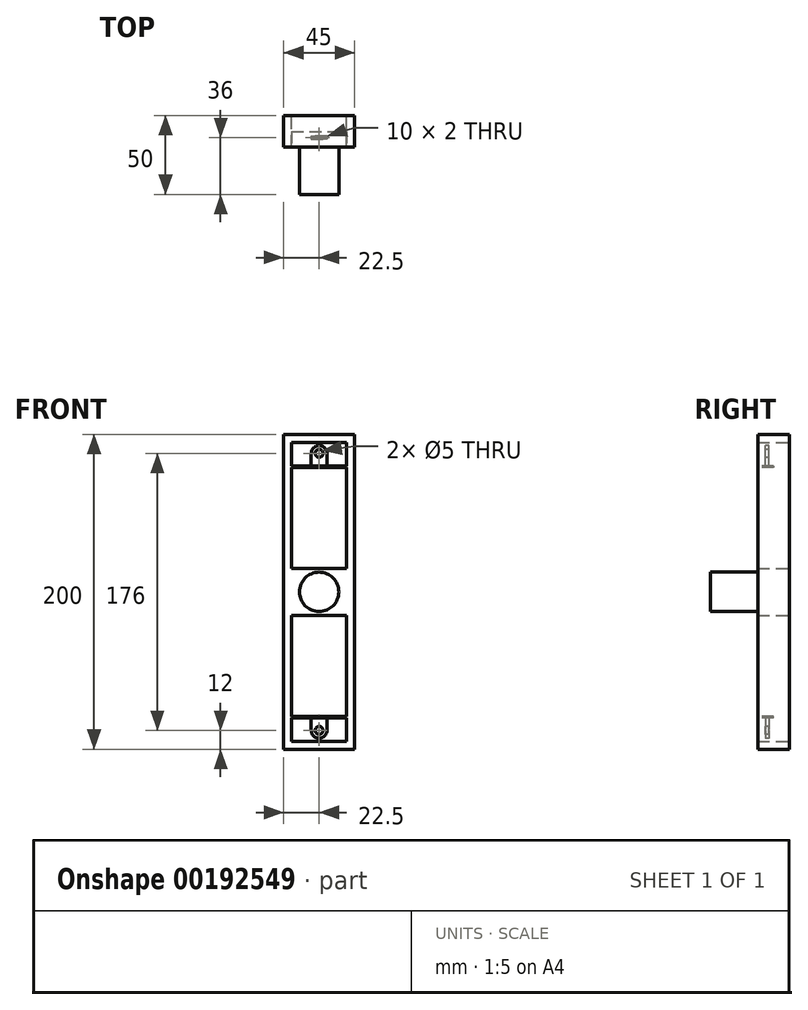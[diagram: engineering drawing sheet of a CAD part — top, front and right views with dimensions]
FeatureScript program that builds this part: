
annotation { "Feature Type Name" : "Feature", "Feature Type Description" : "" }
export const myFeature = defineFeature(function(context is Context, id is Id, definition is map)
    precondition{}
    {
        {
            var Q0;
            Q0=qCreatedBy(makeId("Front.planeOp"),FACE);
            var sketch = newSketch(context, id + "F0", { "sketchPlane" : qUnion([Q0])});
            skCircle(sketch, "E0", {"center": v(0, 0) * mm, "radius": 12.5 * mm});
            skSolve(sketch);
        }
        {
            var Q0;
            Q0=qSketchRegion(id+"F0",true);
            extrude(context, id + "F1", {"entities" : qUnion([Q0]), "depth" : 40 * mm});
        }
        {
            var Q0;
            Q0=qCreatedBy(makeId("Front.planeOp"),FACE);
            cPlane(context, id + "F2", {"entities" : qUnion([Q0]), "cplaneType" : CPlaneType.OFFSET, "offset" : 10 * mm, "width" : 150 * mm, "height" : 150 * mm});
        }
        {
            var Q0;
            Q0=qCreatedBy(id+"F2.planeOp",FACE);
            var sketch = newSketch(context, id + "F3", { "sketchPlane" : qUnion([Q0])});
            skLineSegment(sketch, "E1.bottom", {"start": v(-22.5, -100) * mm, "end": v(22.5, -100) * mm});
            skLineSegment(sketch, "E1.top", {"start": v(-22.5, 100) * mm, "end": v(22.5, 100) * mm});
            skLineSegment(sketch, "E1.left", {"start": v(-22.5, -100) * mm, "end": v(-22.5, 100) * mm});
            skLineSegment(sketch, "E1.right", {"start": v(22.5, -100) * mm, "end": v(22.5, 100) * mm});
            skPoint(sketch, "E1.middle", {"position": v(0, 0) * mm});
            skSolve(sketch);
        }
        {
            var Q0;
            Q0=qSketchRegion(id+"F3",true);
            extrude(context, id + "F4", {"entities" : qUnion([Q0]), "operationType" : NewBodyOperationType.ADD, "oppositeDirection" : true, "depth" : 20 * mm});
        }
        {
            var Q0;
            Q0=makeQuery(id+"F4.opExtrude","CAP_FACE",FACE,{"disambiguationData":[OSD([sQuery(id+"F3.wireOp",EDGE,"E1.bottom"),sQuery(id+"F3.wireOp",EDGE,"E1.top"),sQuery(id+"F3.wireOp",EDGE,"E1.left"),sQuery(id+"F3.wireOp",EDGE,"E1.right")])],"isStart":false});
            var sketch = newSketch(context, id + "F5", { "sketchPlane" : qUnion([Q0])});
            skLineSegment(sketch, "E2.bottom", {"start": v(-17.5, 95) * mm, "end": v(17.5, 95) * mm});
            skLineSegment(sketch, "E2.top", {"start": v(-17.5, 15) * mm, "end": v(17.5, 15) * mm});
            skLineSegment(sketch, "E2.left", {"start": v(-17.5, 95) * mm, "end": v(-17.5, 15) * mm});
            skLineSegment(sketch, "E2.right", {"start": v(17.5, 95) * mm, "end": v(17.5, 15) * mm});
            skLineSegment(sketch, "E3.bottom", {"start": v(-17.5, -15) * mm, "end": v(17.5, -15) * mm});
            skLineSegment(sketch, "E3.top", {"start": v(-17.5, -95) * mm, "end": v(17.5, -95) * mm});
            skLineSegment(sketch, "E3.left", {"start": v(-17.5, -15) * mm, "end": v(-17.5, -95) * mm});
            skLineSegment(sketch, "E3.right", {"start": v(17.5, -15) * mm, "end": v(17.5, -95) * mm});
            skSolve(sketch);
        }
        {
            var Q0;
            Q0 = qSketchRegion(id + "F5", true);
            extrude(context, id + "F6", {"entities" : qUnion([Q0]), "operationType" : NewBodyOperationType.REMOVE, "oppositeDirection" : true, "depth" : 25 * mm});
        }
        {
            var Q0;
            Q0=qCreatedBy(makeId("Top.planeOp"),FACE);
            cPlane(context, id + "F7", {"entities" : qUnion([Q0]), "cplaneType" : CPlaneType.OFFSET, "offset" : 80 * mm, "width" : 150 * mm, "height" : 150 * mm});
        }
        {
            var Q0;
            Q0=qCreatedBy(makeId("Top.planeOp"),FACE);
            cPlane(context, id + "F8", {"entities" : qUnion([Q0]), "cplaneType" : CPlaneType.OFFSET, "offset" : 80 * mm, "oppositeDirection" : true, "width" : 150 * mm, "height" : 150 * mm});
        }
        {
            var Q0;
            Q0=qCreatedBy(id+"F7.planeOp",FACE);
            var sketch = newSketch(context, id + "F9", { "sketchPlane" : qUnion([Q0])});
            skLineSegment(sketch, "E4.bottom", {"start": v(-22.5, -10) * mm, "end": v(22.5, -10) * mm});
            skLineSegment(sketch, "E4.top", {"start": v(-22.5, 0) * mm, "end": v(22.5, 0) * mm});
            skLineSegment(sketch, "E4.left", {"start": v(-22.5, -10) * mm, "end": v(-22.5, 0) * mm});
            skLineSegment(sketch, "E4.right", {"start": v(22.5, -10) * mm, "end": v(22.5, 0) * mm});
            skSolve(sketch);
        }
        {
            var Q0;
            Q0 = qSketchRegion(id + "F9", true);
            extrude(context, id + "F10", {"entities" : qUnion([Q0]), "operationType" : NewBodyOperationType.ADD, "oppositeDirection" : true, "depth" : 1 * mm});
        }
        {
            var Q0;
            Q0=qCreatedBy(id+"F8.planeOp",FACE);
            var sketch = newSketch(context, id + "F11", { "sketchPlane" : qUnion([Q0])});
            skLineSegment(sketch, "E5.bottom", {"start": v(-22.5, 0) * mm, "end": v(22.5, 0) * mm});
            skLineSegment(sketch, "E5.top", {"start": v(-22.5, -10) * mm, "end": v(22.5, -10) * mm});
            skLineSegment(sketch, "E5.left", {"start": v(-22.5, 0) * mm, "end": v(-22.5, -10) * mm});
            skLineSegment(sketch, "E5.right", {"start": v(22.5, 0) * mm, "end": v(22.5, -10) * mm});
            skSolve(sketch);
        }
        {
            var Q0;
            Q0 = qSketchRegion(id + "F11", true);
            extrude(context, id + "F12", {"entities" : qUnion([Q0]), "operationType" : NewBodyOperationType.ADD, "depth" : 1 * mm});
        }
        {
            var Q0;
            Q0=qCreatedBy(makeId("Front.planeOp"),FACE);
            cPlane(context, id + "F13", {"entities" : qUnion([Q0]), "cplaneType" : CPlaneType.OFFSET, "offset" : 5 * mm, "width" : 150 * mm, "height" : 150 * mm});
        }
        {
            var Q0;
            Q0=qCreatedBy(id+"F13.planeOp",FACE);
            var sketch = newSketch(context, id + "F14", { "sketchPlane" : qUnion([Q0])});
            skLineSegment(sketch, "E6", {"start": v(-5, 80) * mm, "end": v(-5, 88) * mm});
            skArc(sketch, "E7", {"start": v(5, 88) * mm, "mid": v(0, 93) * mm, "end": v(-5, 88) * mm});
            skLineSegment(sketch, "E8", {"start": v(5, 88) * mm, "end": v(5, 80) * mm});
            skLineSegment(sketch, "E9", {"start": v(-5, -80) * mm, "end": v(-5, -88) * mm});
            skArc(sketch, "E10", {"start": v(-5, -88) * mm, "mid": v(0, -93) * mm, "end": v(5, -88) * mm});
            skLineSegment(sketch, "E11", {"start": v(5, -88) * mm, "end": v(5, -80) * mm});
            skLineSegment(sketch, "E12", {"start": v(-5, 80) * mm, "end": v(5, 80) * mm});
            skLineSegment(sketch, "E13", {"start": v(-5, -80) * mm, "end": v(5, -80) * mm});
            skSolve(sketch);
        }
        {
            var Q0;
            Q0 = qSketchRegion(id + "F14", true);
            extrude(context, id + "F15", {"entities" : qUnion([Q0]), "oppositeDirection" : true, "depth" : 2 * mm});
        }
        {
            var Q0;
            Q0=makeQuery(id+"F1.opExtrude","SWEPT_BODY",BODY,{"disambiguationData":[OSD([sQuery(id+"F0.wireOp",EDGE,"E0")])]});
            var Q1;
            Q1=makeQuery(id+"F15.opExtrude","SWEPT_BODY",BODY,{"disambiguationData":[OSD([sQuery(id+"F14.wireOp",EDGE,"E6"),sQuery(id+"F14.wireOp",EDGE,"E7"),sQuery(id+"F14.wireOp",EDGE,"E8"),sQuery(id+"F14.wireOp",EDGE,"E12")])]});
            var Q2;
            Q2=makeQuery(id+"F15.opExtrude","SWEPT_BODY",BODY,{"disambiguationData":[OSD([sQuery(id+"F14.wireOp",EDGE,"E9"),sQuery(id+"F14.wireOp",EDGE,"E10"),sQuery(id+"F14.wireOp",EDGE,"E11"),sQuery(id+"F14.wireOp",EDGE,"E13")])]});
            booleanBodies(context, id + "F16", {"operationType" : BooleanOperationType.UNION, "tools" : qUnion([Q0, Q1, Q2])});
        }
        {
            var Q0;
            Q0=makeQuery(id+"F16.opBoolean","MERGE",FACE,{"derivedFrom":[makeQuery(id+"F12.boolean.opBoolean","MERGE",FACE,{"derivedFrom":[makeQuery(id+"F10.boolean.opBoolean","MERGE",FACE,{"derivedFrom":[makeQuery(id+"F4.opExtrude","CAP_FACE",FACE,{"disambiguationData":[OSD([sQuery(id+"F3.wireOp",EDGE,"E1.bottom"),sQuery(id+"F3.wireOp",EDGE,"E1.top"),sQuery(id+"F3.wireOp",EDGE,"E1.left"),sQuery(id+"F3.wireOp",EDGE,"E1.right")])],"isStart":true}),makeQuery(id+"F10.opExtrude","SWEPT_FACE",FACE,{"disambiguationData":[OSD([sQuery(id+"F9.wireOp",EDGE,"E4.bottom")])]})]}),makeQuery(id+"F12.opExtrude","SWEPT_FACE",FACE,{"disambiguationData":[OSD([sQuery(id+"F11.wireOp",EDGE,"E5.top")])]})]}),makeQuery(id+"F15.opExtrude","CAP_FACE",FACE,{"disambiguationData":[OSD([sQuery(id+"F14.wireOp",EDGE,"E6"),sQuery(id+"F14.wireOp",EDGE,"E7"),sQuery(id+"F14.wireOp",EDGE,"E8"),sQuery(id+"F14.wireOp",EDGE,"E12")])],"isStart":true}),makeQuery(id+"F15.opExtrude","CAP_FACE",FACE,{"disambiguationData":[OSD([sQuery(id+"F14.wireOp",EDGE,"E9"),sQuery(id+"F14.wireOp",EDGE,"E10"),sQuery(id+"F14.wireOp",EDGE,"E11"),sQuery(id+"F14.wireOp",EDGE,"E13")])],"isStart":true})]});
            var sketch = newSketch(context, id + "F17", { "sketchPlane" : qUnion([Q0])});
            skCircle(sketch, "E14", {"center": v(0, -88) * mm, "radius": 2.5 * mm});
            skCircle(sketch, "E15", {"center": v(0, 88) * mm, "radius": 2.5 * mm});
            skSolve(sketch);
        }
        {
            var Q0;
            Q0 = qSketchRegion(id + "F17", true);
            extrude(context, id + "F18", {"entities" : qUnion([Q0]), "operationType" : NewBodyOperationType.REMOVE, "endBound" : BoundingType.THROUGH_ALL, "oppositeDirection" : true, "depth" : 25 * mm});
        }
    });
